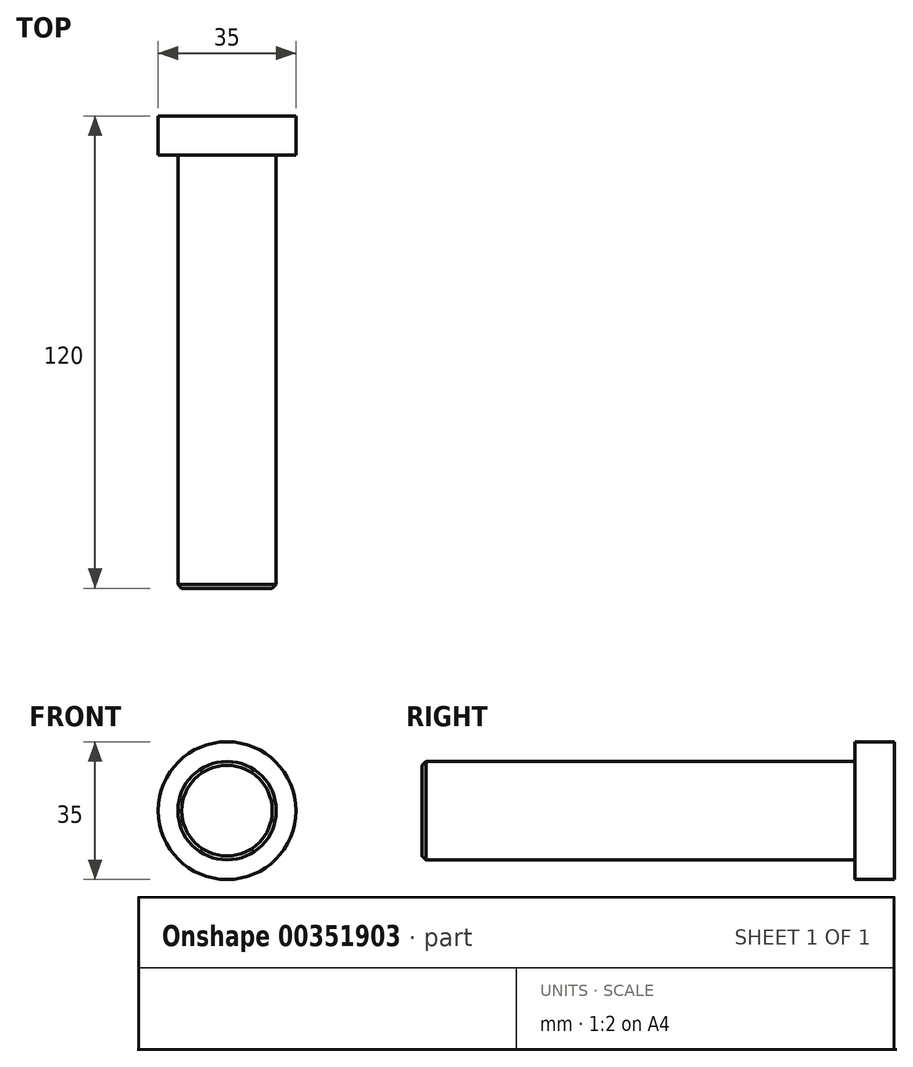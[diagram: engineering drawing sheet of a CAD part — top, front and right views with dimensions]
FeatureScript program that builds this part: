
annotation { "Feature Type Name" : "Feature", "Feature Type Description" : "" }
export const myFeature = defineFeature(function(context is Context, id is Id, definition is map)
    precondition{}
    {
        {
            var Q0;
            Q0=qCreatedBy(makeId("Front.planeOp"),FACE);
            var sketch = newSketch(context, id + "F0", { "sketchPlane" : qUnion([Q0])});
            skCircle(sketch, "E0", {"center": v(0, 0) * mm, "radius": 12.5 * mm});
            skSolve(sketch);
        }
        {
            var Q0;
            Q0 = qSketchRegion(id + "F0", true);
            extrude(context, id + "F1", {"entities" : qUnion([Q0]), "depth" : 120 * mm});
        }
        {
            var Q0;
            Q0=makeQuery(id+"F1.opExtrude","CAP_EDGE",EDGE,{"disambiguationData":[OSD([sQuery(id+"F0.wireOp",EDGE,"E0")])],"isStart":false});
            var Q1;
            Q1=makeQuery(id+"F1.opExtrude","CAP_EDGE",EDGE,{"disambiguationData":[OSD([sQuery(id+"F0.wireOp",EDGE,"E0")])],"isStart":true});
            chamfer(context, id + "F2", {"entities" : qUnion([Q0, Q1]), "width" : 1 * mm, "tangentPropagation" : true});
        }
        {
            var Q0;
            Q0=qCreatedBy(makeId("Front.planeOp"),FACE);
            var sketch = newSketch(context, id + "F3", { "sketchPlane" : qUnion([Q0])});
            skCircle(sketch, "E1", {"center": v(0, 0) * mm, "radius": 17.5 * mm});
            skSolve(sketch);
        }
        {
            var Q0;
            Q0 = qSketchRegion(id + "F3", true);
            extrude(context, id + "F4", {"entities" : qUnion([Q0]), "operationType" : NewBodyOperationType.ADD, "depth" : 10 * mm});
        }
    });
